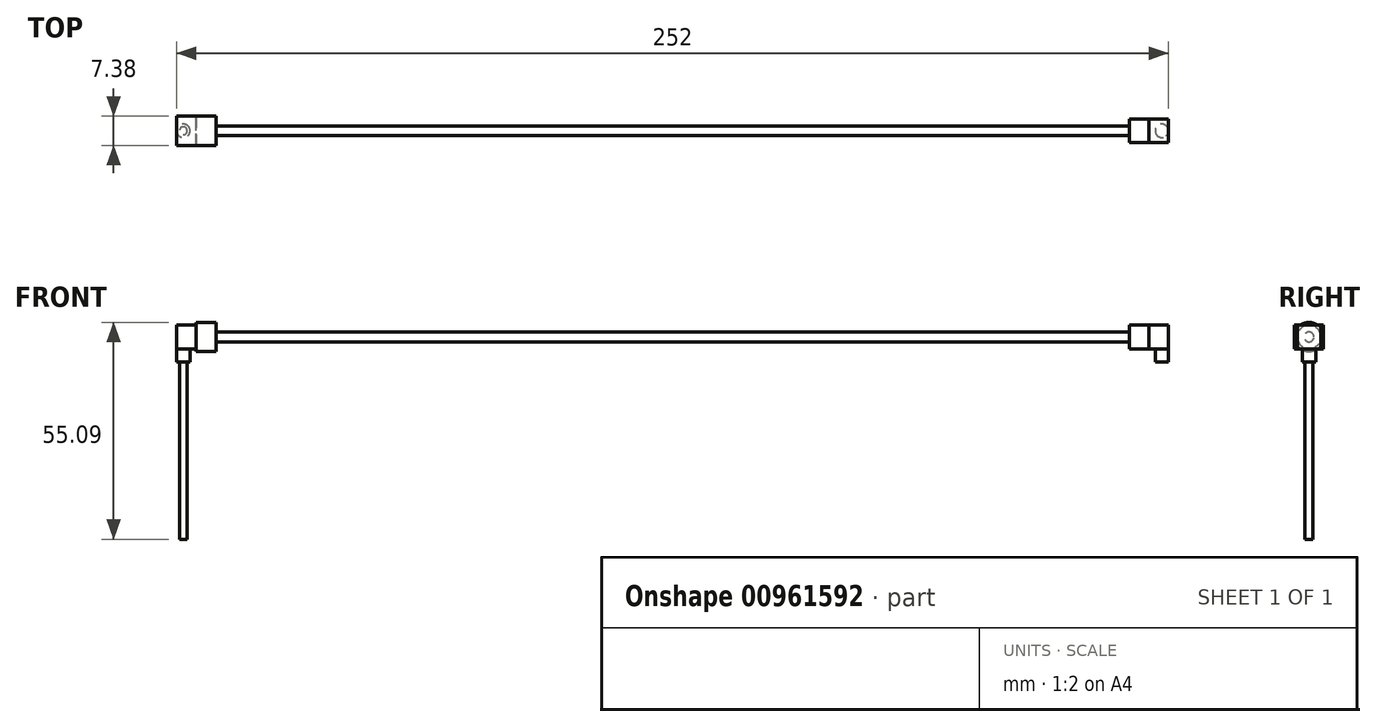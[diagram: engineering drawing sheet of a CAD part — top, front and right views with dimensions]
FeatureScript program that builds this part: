
annotation { "Feature Type Name" : "Feature", "Feature Type Description" : "" }
export const myFeature = defineFeature(function(context is Context, id is Id, definition is map)
    precondition{}
    {
        {
            var Q0;
            Q0=qCreatedBy(makeId("Top.planeOp"),FACE);
            var sketch = newSketch(context, id + "F0", { "sketchPlane" : qUnion([Q0])});
            skLineSegment(sketch, "E0", {"start": v(-126, 1.25) * mm, "end": v(-126, 0) * mm});
            skLineSegment(sketch, "E1", {"start": v(-126, 0) * mm, "end": v(126, 0) * mm});
            skLineSegment(sketch, "E2", {"start": v(126, 0) * mm, "end": v(126, 1.25) * mm});
            skLineSegment(sketch, "E3", {"start": v(126, 1.25) * mm, "end": v(-126, 1.25) * mm});
            skLineSegment(sketch, "E4", {"start": v(126, 0) * mm, "end": v(126, -3) * mm});
            skLineSegment(sketch, "E5", {"start": v(126, 1.25) * mm, "end": v(126, 3) * mm});
            skLineSegment(sketch, "E6", {"start": v(126, 3) * mm, "end": v(121, 3) * mm});
            skLineSegment(sketch, "E7", {"start": v(121, -3) * mm, "end": v(126, -3) * mm});
            skLineSegment(sketch, "E8", {"start": v(121, 3) * mm, "end": v(121, -3) * mm});
            skPoint(sketch, "E9.orphan", {"position": v(116, -3) * mm});
            skPoint(sketch, "E10.orphan", {"position": v(116, 3) * mm});
            skLineSegment(sketch, "E11", {"start": v(121, 3) * mm, "end": v(116, 3) * mm});
            skLineSegment(sketch, "E12", {"start": v(116, 0) * mm, "end": v(116, 3) * mm});
            skLineSegment(sketch, "E13", {"start": v(-126, -3.7) * mm, "end": v(-126, 3.7) * mm});
            skLineSegment(sketch, "E14", {"start": v(-126, -3.7) * mm, "end": v(-121, -3.7) * mm});
            skLineSegment(sketch, "E15", {"start": v(-116, 0) * mm, "end": v(-116, 3.7) * mm});
            skLineSegment(sketch, "E16", {"start": v(-116, 3.7) * mm, "end": v(-121, 3.7) * mm});
            skLineSegment(sketch, "E17", {"start": v(-121, 3.7) * mm, "end": v(-126, 3.7) * mm});
            skLineSegment(sketch, "E18", {"start": v(-121, -3.7) * mm, "end": v(-121, 0) * mm});
            skLineSegment(sketch, "E19", {"start": v(-121, 0) * mm, "end": v(-121, 1.25) * mm});
            skLineSegment(sketch, "E20", {"start": v(-121, 1.25) * mm, "end": v(-121, 3.7) * mm});
            skSolve(sketch);
        }
        {
            var Q0;
            {var subQ0=sQuery(id+"F0.wireOp",EDGE,"E4");Q0=makeQuery(id+"F0.imprint","IMPRINT",FACE,{"disambiguationData":[TD([[makeQuery(id+"F0.imprint","IMPRINT",EDGE,{"derivedFrom":subQ0}),-1.0]])]});}
            var Q1;
            {var subQ0=sQuery(id+"F0.wireOp",EDGE,"E2");Q1=makeQuery(id+"F0.imprint","IMPRINT",FACE,{"disambiguationData":[TD([[makeQuery(id+"F0.imprint","IMPRINT",EDGE,{"derivedFrom":subQ0}),1.0]])]});}
            var Q2;
            {var subQ0=sQuery(id+"F0.wireOp",EDGE,"E5");Q2=makeQuery(id+"F0.imprint","IMPRINT",FACE,{"disambiguationData":[TD([[makeQuery(id+"F0.imprint","IMPRINT",EDGE,{"derivedFrom":subQ0}),1.0]])]});}
            var Q3;
            {var subQ4=sQuery(id+"F0.wireOp",EDGE,"E14");Q3=makeQuery(id+"F0.imprint","IMPRINT",FACE,{"disambiguationData":[TD([[makeQuery(id+"F0.imprint","IMPRINT",EDGE,{"derivedFrom":subQ4}),1.0]])]});}
            var Q4;
            {var subQ3=sQuery(id+"F0.wireOp",EDGE,"E19");Q4=makeQuery(id+"F0.imprint","IMPRINT",FACE,{"disambiguationData":[TD([[makeQuery(id+"F0.imprint","IMPRINT",EDGE,{"derivedFrom":subQ3}),1.0]])]});}
            var Q5;
            {var subQ4=sQuery(id+"F0.wireOp",EDGE,"E17");Q5=makeQuery(id+"F0.imprint","IMPRINT",FACE,{"disambiguationData":[TD([[makeQuery(id+"F0.imprint","IMPRINT",EDGE,{"derivedFrom":subQ4}),1.0]])]});}
            extrude(context, id + "F1", {"entities" : qUnion([Q0, Q1, Q2, Q3, Q4, Q5]), "endBound" : BoundingType.SYMMETRIC, "depth" : 6 * mm, "offsetDistance" : 25 * mm});
        }
        {
            var Q0;
            {var subQ3=sQuery(id+"F0.wireOp",EDGE,"E19");Q0=makeQuery(id+"F0.imprint","IMPRINT",FACE,{"disambiguationData":[TD([[makeQuery(id+"F0.imprint","IMPRINT",EDGE,{"derivedFrom":subQ3}),-1.0]])]});}
            var Q1;
            {var subQ4=sQuery(id+"F0.wireOp",EDGE,"E16");Q1=makeQuery(id+"F0.imprint","IMPRINT",FACE,{"disambiguationData":[TD([[makeQuery(id+"F0.imprint","IMPRINT",EDGE,{"derivedFrom":subQ4}),1.0]])]});}
            var Q2;
            {var subQ0=sQuery(id+"F0.wireOp",EDGE,"E12");var subQ1=sQuery(id+"F0.wireOp",EDGE,"E1");var subQ2=makeQuery(id+"F0.imprint","INTERSECT",VERTEX,{"derivedFrom":[subQ1,subQ0]});Q2=makeQuery(id+"F0.imprint","IMPRINT",FACE,{"disambiguationData":[TD([[makeQuery(id+"F0.imprint","IMPRINT",EDGE,{"disambiguationData":[TD([[subQ2,1.0]])],"derivedFrom":subQ1}),1.0]])]});}
            var Q3;
            {var subQ5=sQuery(id+"F0.wireOp",EDGE,"E11");Q3=makeQuery(id+"F0.imprint","IMPRINT",FACE,{"disambiguationData":[TD([[makeQuery(id+"F0.imprint","IMPRINT",EDGE,{"derivedFrom":subQ5}),1.0]])]});}
            var Q4;
            {var subQ0=sQuery(id+"F0.wireOp",EDGE,"E12");var subQ1=sQuery(id+"F0.wireOp",EDGE,"E1");var subQ2=makeQuery(id+"F0.imprint","INTERSECT",VERTEX,{"derivedFrom":[subQ1,subQ0]});Q4=makeQuery(id+"F0.imprint","IMPRINT",FACE,{"disambiguationData":[TD([[makeQuery(id+"F0.imprint","IMPRINT",EDGE,{"disambiguationData":[TD([[subQ2,-1.0]])],"derivedFrom":subQ1}),1.0]])]});}
            var Q5;
            Q5=sQuery(id+"F0.wireOp",EDGE,"E1");
            revolve(context, id + "F2", {"surfaceOperationType" : NewSurfaceOperationType.NEW, "entities" : qUnion([Q0, Q1, Q2, Q3, Q4]), "axis" : qUnion([Q5]), "revolveType" : RevolveType.FULL});
        }
        {
            var Q0;
            Q0=makeQuery(id+"F2.opRevolve","SWEPT_BODY",BODY,{"disambiguationData":[OSD([sQuery(id+"F0.wireOp",EDGE,"E0"),sQuery(id+"F0.wireOp",EDGE,"E1"),sQuery(id+"F0.wireOp",EDGE,"E3"),sQuery(id+"F0.wireOp",EDGE,"E8"),sQuery(id+"F0.wireOp",EDGE,"E11"),sQuery(id+"F0.wireOp",EDGE,"E12")])]});
            var Q1;
            Q1=makeQuery(id+"F1.opExtrude","SWEPT_BODY",BODY,{"disambiguationData":[OSD([sQuery(id+"F0.wireOp",EDGE,"E2"),sQuery(id+"F0.wireOp",EDGE,"E4"),sQuery(id+"F0.wireOp",EDGE,"E5"),sQuery(id+"F0.wireOp",EDGE,"E7"),sQuery(id+"F0.wireOp",EDGE,"E6"),sQuery(id+"F0.wireOp",EDGE,"E8")])]});
            booleanBodies(context, id + "F3", {"operationType" : BooleanOperationType.UNION, "tools" : qUnion([Q0, Q1])});
        }
        {
            var Q0;
            Q0=makeQuery(id+"F1.opExtrude","CAP_FACE",FACE,{"disambiguationData":[OSD([sQuery(id+"F0.wireOp",EDGE,"E2"),sQuery(id+"F0.wireOp",EDGE,"E4"),sQuery(id+"F0.wireOp",EDGE,"E5"),sQuery(id+"F0.wireOp",EDGE,"E7"),sQuery(id+"F0.wireOp",EDGE,"E6"),sQuery(id+"F0.wireOp",EDGE,"E8")])],"isStart":true});
            var sketch = newSketch(context, id + "F4", { "sketchPlane" : qUnion([Q0])});
            skCircle(sketch, "E21", {"center": v(124.3, 0) * mm, "radius": 1.7 * mm});
            skSolve(sketch);
        }
        {
            var Q0;
            Q0=makeQuery(id+"F1.opExtrude","CAP_FACE",FACE,{"disambiguationData":[OSD([sQuery(id+"F0.wireOp",EDGE,"E13"),sQuery(id+"F0.wireOp",EDGE,"E14"),sQuery(id+"F0.wireOp",EDGE,"E17"),sQuery(id+"F0.wireOp",EDGE,"E18"),sQuery(id+"F0.wireOp",EDGE,"E19"),sQuery(id+"F0.wireOp",EDGE,"E20")])],"isStart":true});
            var sketch = newSketch(context, id + "F5", { "sketchPlane" : qUnion([Q0])});
            skCircle(sketch, "E22", {"center": v(-124.3, 0) * mm, "radius": 1.7 * mm});
            skPoint(sketch, "E22.centerSnap0", {"position": v(-126, 0) * mm});
            skSolve(sketch);
        }
        {
            var Q0;
            Q0=makeQuery(id+"F5.imprint","IMPRINT",FACE,{"disambiguationData":[TD([[makeQuery(id+"F5.imprint","IMPRINT",EDGE,{"derivedFrom":sQuery(id+"F5.wireOp",EDGE,"E22")}),1.0]])]});
            var Q1;
            Q1=makeQuery(id+"F4.imprint","IMPRINT",FACE,{"disambiguationData":[TD([[makeQuery(id+"F4.imprint","IMPRINT",EDGE,{"derivedFrom":sQuery(id+"F4.wireOp",EDGE,"E21")}),1.0]])]});
            extrude(context, id + "F6", {"entities" : qUnion([Q0, Q1]), "operationType" : NewBodyOperationType.ADD, "depth" : 3.4 * mm, "offsetDistance" : 25 * mm});
        }
        {
            var Q0;
            Q0=makeQuery(id+"F6.opExtrude","CAP_FACE",FACE,{"disambiguationData":[OSD([sQuery(id+"F5.wireOp",EDGE,"E22")])],"isStart":false});
            var sketch = newSketch(context, id + "F7", { "sketchPlane" : qUnion([Q0])});
            skCircle(sketch, "E23", {"center": v(-124.3, 0) * mm, "radius": 1 * mm});
            skSolve(sketch);
        }
        {
            var Q0;
            Q0=makeQuery(id+"F7.imprint","IMPRINT",FACE,{"disambiguationData":[TD([[makeQuery(id+"F7.imprint","IMPRINT",EDGE,{"derivedFrom":sQuery(id+"F7.wireOp",EDGE,"E23")}),1.0]])]});
            extrude(context, id + "F8", {"entities" : qUnion([Q0]), "operationType" : NewBodyOperationType.ADD, "depth" : 45 * mm, "offsetDistance" : 25 * mm});
        }
    });
